# Revit family: Haworth_Masters_Modular_Shell
name_source: partatom
category: Furniture Systems
revit_build: Autodesk Revit 2018 (Build: 20170223_1515(x64)
units: mm (PartAtom-declared; Revit-internal decimal feet)

## family parameters
Always vertical = Yes
Cut with Voids When Loaded = No
OmniClass Number = 23.40.70.14.64.21
OmniClass Title = Systems Furniture
Part Type = Normal
Room Calculation Point = No
Round Connector Dimension = Use Diameter
Shared = No
Work Plane-Based = No

## types (5) — shared parameters
Actual Depth = 24"
Actual Height = 29 1/8"
Actual Width = 72"
Assembly Code = E2020200
Cabinet Finish = Haworth _ Wood _ White Oak
Custom Size = No
Depth = 24"
Description = Haworth - Masters - Modular Shell
Edge Finish = Haworth _ Wood _ White Oak
End Panel Depth = 23 1/4"
Manufacturer = Haworth
Max. Depth = 36"
Max. Width = 120"
Min. Depth = 19"
Min. Width = 30"
Model = Haworth - Masters - Modular Shell
Modesty Single = No
One And A Half High = Yes
One High = No
Partial Depth Panel = No
Revision Number = 2
Size = Verify Final Dim. w/ Haworth
Standard Depths = 19,24,30 in.
Standard Widths = 30,36,42,48,54,60,66,72,78,84,90,96,102,108,114,120 in.
Support Height = 21 7/8"
Sustainability Info = http://www.haworth.com
T-Support End Placement = 12"
URL = www.haworth.com
URL - Product = http://www.haworth.com
Warranty = http://www.haworth.com
Width = 72"
Worksurface Finish = Haworth _ Wood _ White Oak

## per-type parameters (varying)
| type | End Panel Left | End Panel Right | L-Support Left | L-Support Right | Modesty Double | One High Limit | T-Support Intermediate | T-Support Left | T-Support Right | Two High | Work Surface |
| Surface Only | No | No | No | No | No | No | No | No | No | Yes | Yes |
| Full Overlay Modesty | Yes | Yes | No | No | No | No | No | Yes | Yes | No | No |
| Hinged Modesty | Yes | Yes | Yes | Yes | Yes | Yes | Yes | No | No | Yes | Yes |
| T-Support | Yes | Yes | No | No | No | No | No | Yes | Yes | Yes | Yes |
| L-Support | Yes | Yes | Yes | Yes | No | No | No | No | No | Yes | Yes |

## geometry (parser evidence)
native form markers: Sweep x2
no freeform markers — native parametric forms only
